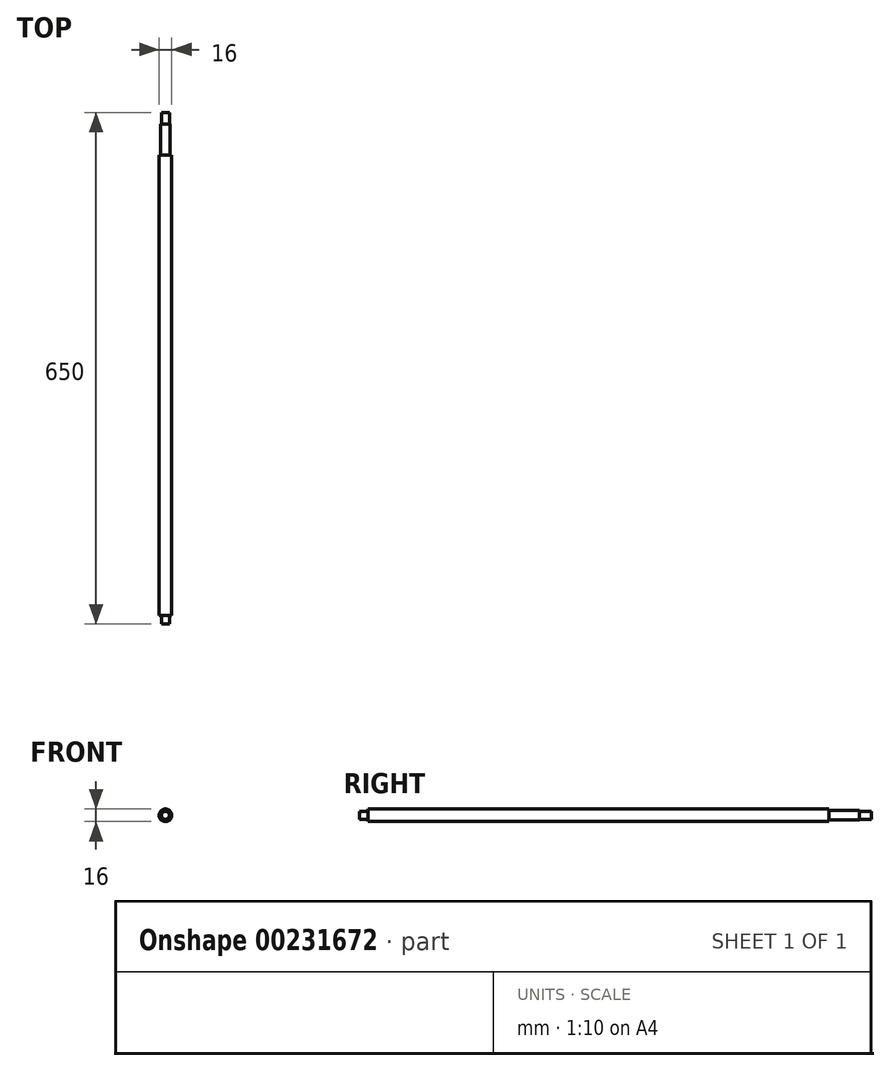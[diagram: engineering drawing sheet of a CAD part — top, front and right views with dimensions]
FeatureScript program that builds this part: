
annotation { "Feature Type Name" : "Feature", "Feature Type Description" : "" }
export const myFeature = defineFeature(function(context is Context, id is Id, definition is map)
    precondition{}
    {
        {
            var Q0;
            Q0=qCreatedBy(makeId("Front.planeOp"),FACE);
            var sketch = newSketch(context, id + "F0", { "sketchPlane" : qUnion([Q0])});
            skCircle(sketch, "E0", {"center": v(0, 0) * mm, "radius": 5 * mm});
            skSolve(sketch);
        }
        {
            var Q0;
            Q0 = qSketchRegion(id + "F0", true);
            extrude(context, id + "F1", {"entities" : qUnion([Q0]), "depth" : 15 * mm});
        }
        {
            var Q0;
            Q0=makeQuery(id+"F1.opExtrude","CAP_FACE",FACE,{"disambiguationData":[OSD([sQuery(id+"F0.wireOp",EDGE,"E0")])],"isStart":false});
            var sketch = newSketch(context, id + "F2", { "sketchPlane" : qUnion([Q0])});
            skCircle(sketch, "E1", {"center": v(0, 0) * mm, "radius": 6 * mm});
            skSolve(sketch);
        }
        {
            var Q0;
            Q0 = qSketchRegion(id + "F2", true);
            extrude(context, id + "F3", {"entities" : qUnion([Q0]), "operationType" : NewBodyOperationType.ADD, "depth" : 39 * mm});
        }
        {
            var Q0;
            Q0=makeQuery(id+"F3.opExtrude","CAP_FACE",FACE,{"disambiguationData":[OSD([sQuery(id+"F2.wireOp",EDGE,"E1")])],"isStart":false});
            var sketch = newSketch(context, id + "F4", { "sketchPlane" : qUnion([Q0])});
            skCircle(sketch, "E2", {"center": v(0, 0) * mm, "radius": 8 * mm});
            skSolve(sketch);
        }
        {
            var Q0;
            Q0 = qSketchRegion(id + "F4", true);
            extrude(context, id + "F5", {"entities" : qUnion([Q0]), "operationType" : NewBodyOperationType.ADD, "depth" : 585 * mm});
        }
        {
            var Q0;
            Q0=makeQuery(id+"F5.opExtrude","CAP_FACE",FACE,{"disambiguationData":[OSD([sQuery(id+"F4.wireOp",EDGE,"E2")])],"isStart":false});
            var sketch = newSketch(context, id + "F6", { "sketchPlane" : qUnion([Q0])});
            skCircle(sketch, "E3", {"center": v(0, 0) * mm, "radius": 5 * mm});
            skSolve(sketch);
        }
        {
            var Q0;
            Q0 = qSketchRegion(id + "F6", true);
            extrude(context, id + "F7", {"entities" : qUnion([Q0]), "operationType" : NewBodyOperationType.ADD, "depth" : 11 * mm});
        }
    });
